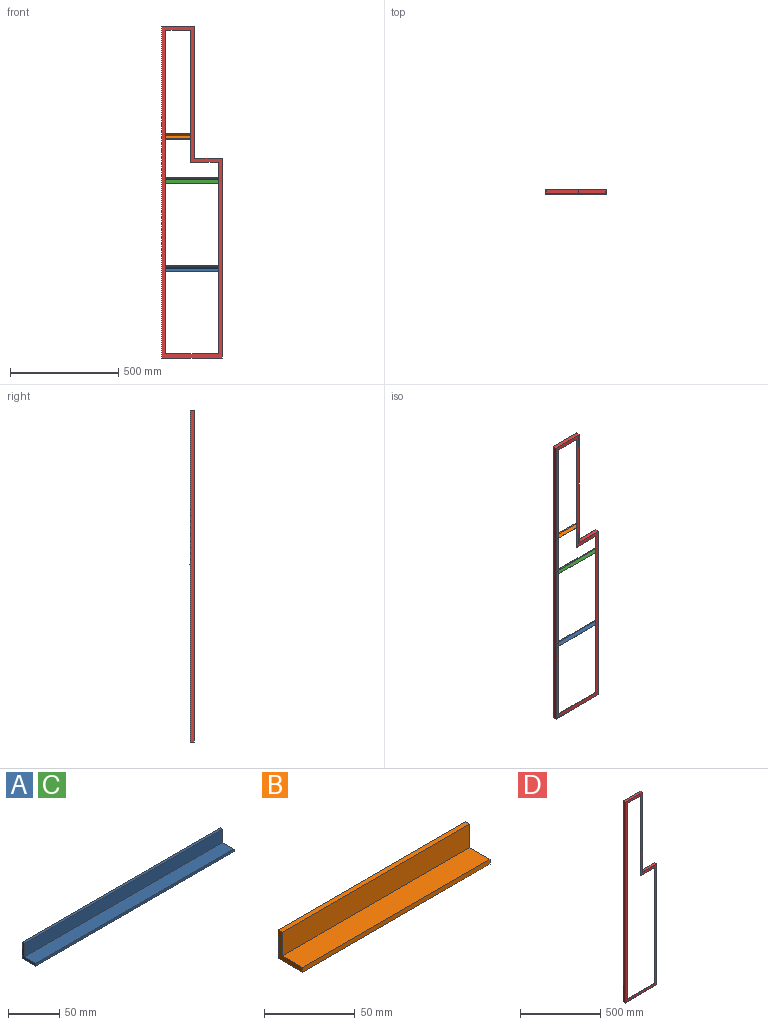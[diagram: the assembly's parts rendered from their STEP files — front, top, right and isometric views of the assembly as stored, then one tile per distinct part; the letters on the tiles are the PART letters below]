
ASSEMBLY  parts=4 mates=3
PART A: 8 faces, bbox 273.1x19.1x19.1 mm
  f0: plane 273.05x3.18mm, normal (0,0,1), area 866.9mm2, adj f1,f5,f6,f7
  f1: plane 273.05x15.88mm, normal (0,-1,0), area 4334.7mm2, adj f0,f2,f6,f7
  f2: plane 273.05x15.88mm, normal (0,0,1), area 4334.7mm2, adj f1,f3,f6,f7
  f3: plane 273.05x3.18mm, normal (0,-1,0), area 866.9mm2, adj f2,f4,f6,f7
  f4: plane 273.05x19.05mm, normal (0,0,-1), area 5201.6mm2, adj f3,f5,f6,f7
  f5: plane 273.05x19.05mm, normal (0,1,0), area 5201.6mm2, adj f0,f4,f6,f7
  f6: plane 19.05x19.05mm, normal (1,0,0), area 110.9mm2, adj f0,f1,f2,f3,f4,f5
  f7: plane 19.05x19.05mm, normal (-1,0,0), area 110.9mm2, adj f0,f1,f2,f3,f4,f5
PART B: 8 faces, bbox 146.1x19.1x19.1 mm
  f0: plane 146.05x3.18mm, normal (0,0,1), area 463.7mm2, adj f1,f5,f6,f7
  f1: plane 146.05x15.88mm, normal (0,-1,0), area 2318.5mm2, adj f0,f2,f6,f7
  f2: plane 146.05x15.88mm, normal (0,0,1), area 2318.5mm2, adj f1,f3,f6,f7
  f3: plane 146.05x3.18mm, normal (0,-1,0), area 463.7mm2, adj f2,f4,f6,f7
  f4: plane 146.05x19.05mm, normal (0,0,-1), area 2782.3mm2, adj f3,f5,f6,f7
  f5: plane 146.05x19.05mm, normal (0,1,0), area 2782.3mm2, adj f0,f4,f6,f7
  f6: plane 19.05x19.05mm, normal (1,0,0), area 110.9mm2, adj f0,f1,f2,f3,f4,f5
  f7: plane 19.05x19.05mm, normal (-1,0,0), area 110.9mm2, adj f0,f1,f2,f3,f4,f5
PART C: same geometry as A
PART D: 21 faces, bbox 279.4x19.1x1530.4 mm
  f0: plane 1524x273.05mm, normal (0,1,0), area 56048.3mm2, adj f6,f7,f8,f9,f10,f11,f14,f15
  f1: plane 127x19.05mm, normal (0,0,1), area 2419.3mm2, adj f2,f12,f13,f20
  f2: plane 609.6x19.05mm, normal (1,0,0), area 11612.9mm2, adj f1,f3,f13,f20
  f3: plane 152.4x19.05mm, normal (0,0,1), area 2903.2mm2, adj f2,f4,f13,f20
  f4: plane 1530.35x19.05mm, normal (-1,0,0), area 29153.2mm2, adj f3,f5,f13,f20
  f5: plane 279.4x19.05mm, normal (0,0,-1), area 5322.6mm2, adj f4,f12,f13,f20
  f6: plane 127x3.18mm, normal (0,0,-1), area 403.2mm2, adj f0,f7,f11,f13
  f7: plane 882.65x3.18mm, normal (-1,0,0), area 2802.4mm2, adj f0,f6,f8,f13
  f8: plane 241.3x3.18mm, normal (0,0,1), area 766.1mm2, adj f0,f7,f9,f13
  f9: plane 1492.25x3.18mm, normal (1,0,0), area 4737.9mm2, adj f0,f8,f10,f13
  f10: plane 114.3x3.18mm, normal (0,0,-1), area 362.9mm2, adj f0,f9,f11,f13
  f11: plane 609.6x3.18mm, normal (-1,0,0), area 1935.5mm2, adj f0,f6,f10,f13
  f12: plane 920.75x19.05mm, normal (1,0,0), area 17540.3mm2, adj f1,f5,f13,f20
  f13: plane 1530.35x279.4mm, normal (0,-1,0), area 67499.9mm2, adj f1,f2,f3,f4,f5,f6,f7,f8
  f14: plane 1524x15.88mm, normal (1,0,0), area 24193.5mm2, adj f0,f15,f19,f20
  f15: plane 273.05x15.88mm, normal (0,0,1), area 4334.7mm2, adj f0,f14,f16,f20
  f16: plane 914.4x15.88mm, normal (-1,0,0), area 14516.1mm2, adj f0,f15,f17,f20
  f17: plane 127x15.88mm, normal (0,0,-1), area 2016.1mm2, adj f0,f16,f18,f20
  f18: plane 609.6x15.88mm, normal (-1,0,0), area 9677.4mm2, adj f0,f17,f19,f20
  f19: plane 146.05x15.88mm, normal (0,0,-1), area 2318.5mm2, adj f0,f14,f18,f20
  f20: plane 1530.35x279.4mm, normal (0,1,0), area 11451.6mm2, adj f1,f2,f3,f4,f5,f12,f14,f15
PLACE A rot(axis=(1,0,0),45deg) t=(-149.22,51.64,-508.94)mm
PLACE B rot(axis=(1,0,0),45deg) t=(-149.23,7.79,134.93)mm
PLACE C rot(axis=(1,0,0),50deg) t=(-149.22,52.42,-98.48)mm
PLACE D at identity fixed
MATE ball A.f2 <-> D.f0  axis (0,-0.71,0.71) through (123.83,0,-520.17)mm
MATE ball B.f2 <-> D.f0  axis (0,-0.71,0.71) through (-3.18,0,90.37)mm
MATE ball C.f0 <-> D.f0  axis (0,-0.77,0.64) through (123.83,0,-91.8)mm
